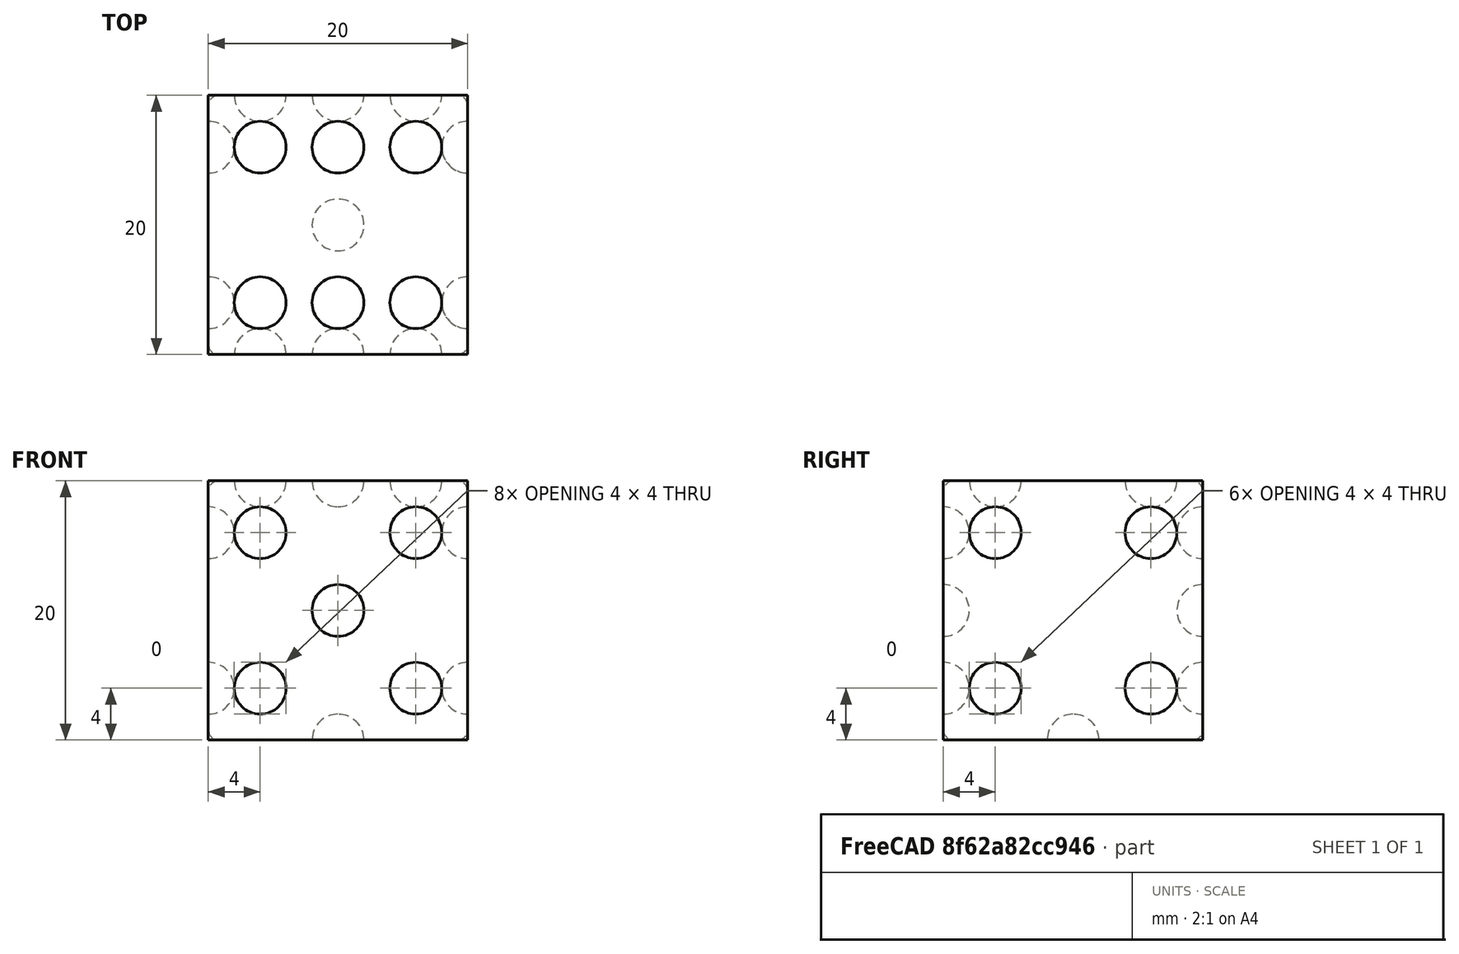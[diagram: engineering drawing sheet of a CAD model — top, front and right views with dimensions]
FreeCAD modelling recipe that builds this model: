
FCSTD DOCUMENT  (FreeCAD 1.0R39285 (Git))
Label: ojt1_t13r02_dado
License: All rights reserved
objects: Part::Sphere×42, Part::Cut×12, Part::MultiFuse×10, Part::Box×2, Part::Fillet×1
note: 67 computed .brp shape members not serialized (recipe doc carries the construction recipe); baked Part::Feature solids carry a one-line shape summary decoded from their .brp

FEATURE [Part::Box] Box  label="Cub"
  AttacherType = Attacher::AttachEngine3D
  Height = 20
  Length = 20
  Width = 20
FEATURE [Part::Sphere] Sphere  label="Esfera"
  Angle1 = -90
  Angle2 = 90
  Angle3 = 360
  AttacherType = Attacher::AttachEngine3D
  Placement = pos=(4,0,4) rot=(0,0,1;0rad)
  Radius = 2
FEATURE [Part::Sphere] Sphere001  label="Esfera001"
  Angle1 = -90
  Angle2 = 90
  Angle3 = 360
  AttacherType = Attacher::AttachEngine3D
  Placement = pos=(16,0,4) rot=(0,0,1;0rad)
  Radius = 2
FEATURE [Part::Sphere] Sphere002  label="Esfera002"
  Angle1 = -90
  Angle2 = 90
  Angle3 = 360
  AttacherType = Attacher::AttachEngine3D
  Placement = pos=(4,0,16) rot=(0,0,1;0rad)
  Radius = 2
FEATURE [Part::Sphere] Sphere003  label="Esfera003"
  Angle1 = -90
  Angle2 = 90
  Angle3 = 360
  AttacherType = Attacher::AttachEngine3D
  Placement = pos=(16,0,16) rot=(0,0,1;0rad)
  Radius = 2
FEATURE [Part::Sphere] Sphere004  label="Esfera004"
  Angle1 = -90
  Angle2 = 90
  Angle3 = 360
  AttacherType = Attacher::AttachEngine3D
  Placement = pos=(10,0,10) rot=(0,0,1;0rad)
  Radius = 2
FEATURE [Part::MultiFuse] Fusion  label="5"
  Refine = true
  Shapes = -> [Sphere,Sphere001,Sphere002,Sphere003,Sphere004]
FEATURE [Part::Sphere] Sphere005  label="Esfera005"
  Angle1 = -90
  Angle2 = 90
  Angle3 = 360
  AttacherType = Attacher::AttachEngine3D
  Placement = pos=(4,4,20) rot=(0,0,1;0rad)
  Radius = 2
FEATURE [Part::Sphere] Sphere006  label="Esfera006"
  Angle1 = -90
  Angle2 = 90
  Angle3 = 360
  AttacherType = Attacher::AttachEngine3D
  Placement = pos=(10,4,20) rot=(0,0,1;0rad)
  Radius = 2
FEATURE [Part::Sphere] Sphere007  label="Esfera007"
  Angle1 = -90
  Angle2 = 90
  Angle3 = 360
  AttacherType = Attacher::AttachEngine3D
  Placement = pos=(16,4,20) rot=(0,0,1;0rad)
  Radius = 2
FEATURE [Part::Sphere] Sphere008  label="Esfera008"
  Angle1 = -90
  Angle2 = 90
  Angle3 = 360
  AttacherType = Attacher::AttachEngine3D
  Placement = pos=(4,16,20) rot=(0,0,1;0rad)
  Radius = 2
FEATURE [Part::Sphere] Sphere009  label="Esfera009"
  Angle1 = -90
  Angle2 = 90
  Angle3 = 360
  AttacherType = Attacher::AttachEngine3D
  Placement = pos=(10,16,20) rot=(0,0,1;0rad)
  Radius = 2
FEATURE [Part::Sphere] Sphere010  label="Esfera010"
  Angle1 = -90
  Angle2 = 90
  Angle3 = 360
  AttacherType = Attacher::AttachEngine3D
  Placement = pos=(16,16,20) rot=(0,0,1;0rad)
  Radius = 2
FEATURE [Part::MultiFuse] Fusion001  label="6"
  Refine = true
  Shapes = -> [Sphere005,Sphere006,Sphere007,Sphere008,Sphere009,Sphere010]
FEATURE [Part::Sphere] Sphere011  label="Esfera011"
  Angle1 = -90
  Angle2 = 90
  Angle3 = 360
  AttacherType = Attacher::AttachEngine3D
  Placement = pos=(20,4,4) rot=(0,0,1;0rad)
  Radius = 2
FEATURE [Part::Sphere] Sphere012  label="Esfera012"
  Angle1 = -90
  Angle2 = 90
  Angle3 = 360
  AttacherType = Attacher::AttachEngine3D
  Placement = pos=(20,4,16) rot=(0,0,1;0rad)
  Radius = 2
FEATURE [Part::Sphere] Sphere013  label="Esfera013"
  Angle1 = -90
  Angle2 = 90
  Angle3 = 360
  AttacherType = Attacher::AttachEngine3D
  Placement = pos=(20,16,4) rot=(0,0,1;0rad)
  Radius = 2
FEATURE [Part::Sphere] Sphere014  label="Esfera014"
  Angle1 = -90
  Angle2 = 90
  Angle3 = 360
  AttacherType = Attacher::AttachEngine3D
  Placement = pos=(20,16,16) rot=(0,0,1;0rad)
  Radius = 2
FEATURE [Part::MultiFuse] Fusion002  label="4"
  Refine = true
  Shapes = -> [Sphere011,Sphere014,Sphere013,Sphere012]
FEATURE [Part::Sphere] Sphere015  label="Esfera015"
  Angle1 = -90
  Angle2 = 90
  Angle3 = 360
  AttacherType = Attacher::AttachEngine3D
  Placement = pos=(4,20,4) rot=(0,0,1;0rad)
  Radius = 2
FEATURE [Part::Sphere] Sphere016  label="Esfera016"
  Angle1 = -90
  Angle2 = 90
  Angle3 = 360
  AttacherType = Attacher::AttachEngine3D
  Placement = pos=(10,20,10) rot=(0,0,1;0rad)
  Radius = 2
FEATURE [Part::Sphere] Sphere017  label="Esfera017"
  Angle1 = -90
  Angle2 = 90
  Angle3 = 360
  AttacherType = Attacher::AttachEngine3D
  Placement = pos=(16,20,16) rot=(0,0,1;0rad)
  Radius = 2
FEATURE [Part::MultiFuse] Fusion003  label="3"
  Refine = true
  Shapes = -> [Sphere017,Sphere015,Sphere016]
FEATURE [Part::Sphere] Sphere018  label="Esfera018"
  Angle1 = -90
  Angle2 = 90
  Angle3 = 360
  AttacherType = Attacher::AttachEngine3D
  Placement = pos=(0,4,4) rot=(0,0,1;0rad)
  Radius = 2
FEATURE [Part::Sphere] Sphere019  label="Esfera019"
  Angle1 = -90
  Angle2 = 90
  Angle3 = 360
  AttacherType = Attacher::AttachEngine3D
  Placement = pos=(0,16,16) rot=(0,0,1;0rad)
  Radius = 2
FEATURE [Part::MultiFuse] Fusion004  label="2"
  Refine = true
  Shapes = -> [Sphere018,Sphere019]
FEATURE [Part::Sphere] Sphere020  label="Esfera020"
  Angle1 = -90
  Angle2 = 90
  Angle3 = 360
  AttacherType = Attacher::AttachEngine3D
  Placement = pos=(10,10,0) rot=(0,0,1;0rad)
  Radius = 2
FEATURE [Part::Cut] Cut
  Base = -> Box
  Refine = true
  Tool = -> Sphere020
FEATURE [Part::Cut] Cut001
  Base = -> Cut
  Refine = true
  Tool = -> Fusion004
FEATURE [Part::Cut] Cut002
  Base = -> Cut001
  Refine = true
  Tool = -> Fusion003
FEATURE [Part::Cut] Cut003
  Base = -> Cut002
  Refine = true
  Tool = -> Fusion002
FEATURE [Part::Cut] Cut004
  Base = -> Cut003
  Refine = true
  Tool = -> Fusion
FEATURE [Part::Cut] Cut005
  Base = -> Cut004
  Refine = true
  Tool = -> Fusion001
FEATURE [Part::Box] Box001  label="Cub001"
  AttacherType = Attacher::AttachEngine3D
  Height = 20
  Length = 20
  Width = 20
FEATURE [Part::Sphere] Sphere021  label="Esfera021"
  Angle1 = -90
  Angle2 = 90
  Angle3 = 360
  AttacherType = Attacher::AttachEngine3D
  Placement = pos=(4,0,4) rot=(0,0,1;0rad)
  Radius = 2
FEATURE [Part::Sphere] Sphere022  label="Esfera022"
  Angle1 = -90
  Angle2 = 90
  Angle3 = 360
  AttacherType = Attacher::AttachEngine3D
  Placement = pos=(16,0,4) rot=(0,0,1;0rad)
  Radius = 2
FEATURE [Part::Sphere] Sphere023  label="Esfera023"
  Angle1 = -90
  Angle2 = 90
  Angle3 = 360
  AttacherType = Attacher::AttachEngine3D
  Placement = pos=(4,0,16) rot=(0,0,1;0rad)
  Radius = 2
FEATURE [Part::Sphere] Sphere024  label="Esfera024"
  Angle1 = -90
  Angle2 = 90
  Angle3 = 360
  AttacherType = Attacher::AttachEngine3D
  Placement = pos=(16,0,16) rot=(0,0,1;0rad)
  Radius = 2
FEATURE [Part::Sphere] Sphere025  label="Esfera025"
  Angle1 = -90
  Angle2 = 90
  Angle3 = 360
  AttacherType = Attacher::AttachEngine3D
  Placement = pos=(10,0,10) rot=(0,0,1;0rad)
  Radius = 2
FEATURE [Part::MultiFuse] Fusion005  label="5001"
  Refine = true
  Shapes = -> [Sphere021,Sphere022,Sphere023,Sphere024,Sphere025]
FEATURE [Part::Sphere] Sphere026  label="Esfera026"
  Angle1 = -90
  Angle2 = 90
  Angle3 = 360
  AttacherType = Attacher::AttachEngine3D
  Placement = pos=(4,4,20) rot=(0,0,1;0rad)
  Radius = 2
FEATURE [Part::Sphere] Sphere027  label="Esfera027"
  Angle1 = -90
  Angle2 = 90
  Angle3 = 360
  AttacherType = Attacher::AttachEngine3D
  Placement = pos=(10,4,20) rot=(0,0,1;0rad)
  Radius = 2
FEATURE [Part::Sphere] Sphere028  label="Esfera028"
  Angle1 = -90
  Angle2 = 90
  Angle3 = 360
  AttacherType = Attacher::AttachEngine3D
  Placement = pos=(16,4,20) rot=(0,0,1;0rad)
  Radius = 2
FEATURE [Part::Sphere] Sphere029  label="Esfera029"
  Angle1 = -90
  Angle2 = 90
  Angle3 = 360
  AttacherType = Attacher::AttachEngine3D
  Placement = pos=(4,16,20) rot=(0,0,1;0rad)
  Radius = 2
FEATURE [Part::Sphere] Sphere030  label="Esfera030"
  Angle1 = -90
  Angle2 = 90
  Angle3 = 360
  AttacherType = Attacher::AttachEngine3D
  Placement = pos=(10,16,20) rot=(0,0,1;0rad)
  Radius = 2
FEATURE [Part::Sphere] Sphere031  label="Esfera031"
  Angle1 = -90
  Angle2 = 90
  Angle3 = 360
  AttacherType = Attacher::AttachEngine3D
  Placement = pos=(16,16,20) rot=(0,0,1;0rad)
  Radius = 2
FEATURE [Part::MultiFuse] Fusion006  label="6001"
  Refine = true
  Shapes = -> [Sphere026,Sphere027,Sphere028,Sphere029,Sphere030,Sphere031]
FEATURE [Part::Sphere] Sphere032  label="Esfera032"
  Angle1 = -90
  Angle2 = 90
  Angle3 = 360
  AttacherType = Attacher::AttachEngine3D
  Placement = pos=(20,4,4) rot=(0,0,1;0rad)
  Radius = 2
FEATURE [Part::Sphere] Sphere033  label="Esfera033"
  Angle1 = -90
  Angle2 = 90
  Angle3 = 360
  AttacherType = Attacher::AttachEngine3D
  Placement = pos=(20,4,16) rot=(0,0,1;0rad)
  Radius = 2
FEATURE [Part::Sphere] Sphere034  label="Esfera034"
  Angle1 = -90
  Angle2 = 90
  Angle3 = 360
  AttacherType = Attacher::AttachEngine3D
  Placement = pos=(20,16,4) rot=(0,0,1;0rad)
  Radius = 2
FEATURE [Part::Sphere] Sphere035  label="Esfera035"
  Angle1 = -90
  Angle2 = 90
  Angle3 = 360
  AttacherType = Attacher::AttachEngine3D
  Placement = pos=(20,16,16) rot=(0,0,1;0rad)
  Radius = 2
FEATURE [Part::MultiFuse] Fusion007  label="4001"
  Refine = true
  Shapes = -> [Sphere032,Sphere035,Sphere034,Sphere033]
FEATURE [Part::Sphere] Sphere036  label="Esfera036"
  Angle1 = -90
  Angle2 = 90
  Angle3 = 360
  AttacherType = Attacher::AttachEngine3D
  Placement = pos=(4,20,4) rot=(0,0,1;0rad)
  Radius = 2
FEATURE [Part::Sphere] Sphere037  label="Esfera037"
  Angle1 = -90
  Angle2 = 90
  Angle3 = 360
  AttacherType = Attacher::AttachEngine3D
  Placement = pos=(10,20,10) rot=(0,0,1;0rad)
  Radius = 2
FEATURE [Part::Sphere] Sphere038  label="Esfera038"
  Angle1 = -90
  Angle2 = 90
  Angle3 = 360
  AttacherType = Attacher::AttachEngine3D
  Placement = pos=(16,20,16) rot=(0,0,1;0rad)
  Radius = 2
FEATURE [Part::MultiFuse] Fusion008  label="3001"
  Refine = true
  Shapes = -> [Sphere038,Sphere036,Sphere037]
FEATURE [Part::Sphere] Sphere039  label="Esfera039"
  Angle1 = -90
  Angle2 = 90
  Angle3 = 360
  AttacherType = Attacher::AttachEngine3D
  Placement = pos=(0,4,4) rot=(0,0,1;0rad)
  Radius = 2
FEATURE [Part::Sphere] Sphere040  label="Esfera040"
  Angle1 = -90
  Angle2 = 90
  Angle3 = 360
  AttacherType = Attacher::AttachEngine3D
  Placement = pos=(0,16,16) rot=(0,0,1;0rad)
  Radius = 2
FEATURE [Part::MultiFuse] Fusion009  label="2001"
  Refine = true
  Shapes = -> [Sphere039,Sphere040]
FEATURE [Part::Sphere] Sphere041  label="Esfera041"
  Angle1 = -90
  Angle2 = 90
  Angle3 = 360
  AttacherType = Attacher::AttachEngine3D
  Placement = pos=(10,10,0) rot=(0,0,1;0rad)
  Radius = 2
FEATURE [Part::Cut] Cut006
  Base = -> Box001
  Refine = true
  Tool = -> Sphere041
FEATURE [Part::Cut] Cut007
  Base = -> Cut006
  Refine = true
  Tool = -> Fusion009
FEATURE [Part::Cut] Cut008
  Base = -> Cut007
  Refine = true
  Tool = -> Fusion008
FEATURE [Part::Cut] Cut009
  Base = -> Cut008
  Refine = true
  Tool = -> Fusion007
FEATURE [Part::Cut] Cut010
  Base = -> Cut009
  Refine = true
  Tool = -> Fusion005
FEATURE [Part::Cut] Cut011
  Base = -> Cut010
  Refine = true
  Tool = -> Fusion006
FEATURE [Part::Fillet] Fillet  label="dau_acabat"
  Base = -> Cut005
  EdgeLinks = -> Cut005 [Edge1,Edge2,Edge3,Edge4,Edge9,Edge10,Edge11,Edge22,Edge23,Edge30,Edge31,Edge33]
  Edges = 12 edges r=0.8: [Edge1,Edge2,Edge3,Edge4,Edge9,Edge10,Edge11,Edge22,Edge23,Edge30,Edge31,Edge33]
